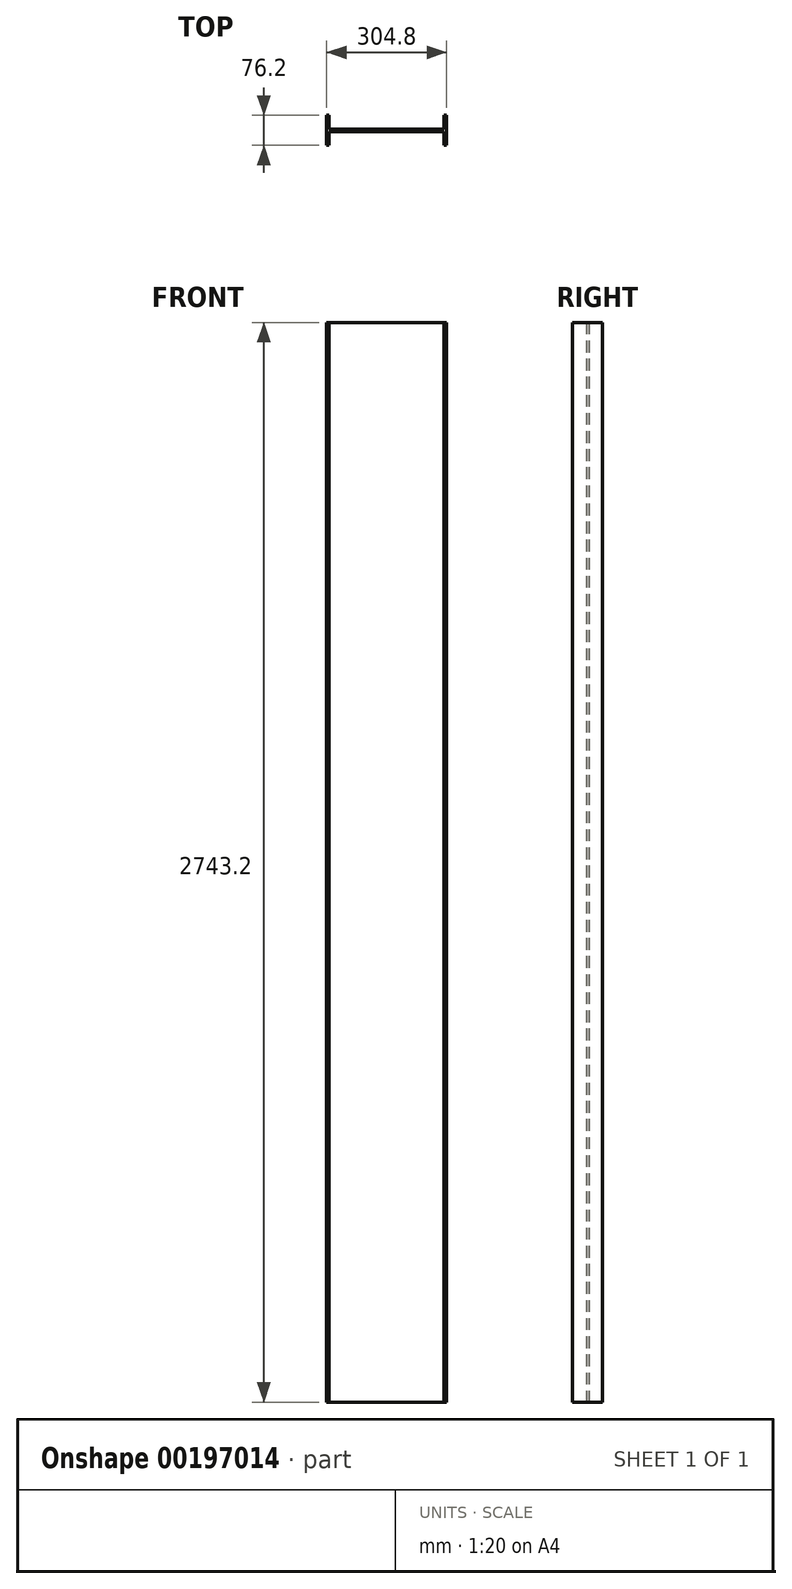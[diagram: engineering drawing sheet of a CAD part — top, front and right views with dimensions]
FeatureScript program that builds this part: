
annotation { "Feature Type Name" : "Feature", "Feature Type Description" : "" }
export const myFeature = defineFeature(function(context is Context, id is Id, definition is map)
    precondition{}
    {
        {
            var Q0;
            Q0=qCreatedBy(makeId("Top.planeOp"),FACE);
            var sketch = newSketch(context, id + "F0", { "sketchPlane" : qUnion([Q0])});
            skLineSegment(sketch, "E0.bottom", {"start": v(0, 0) * mm, "end": v(6.35, 0) * mm});
            skLineSegment(sketch, "E0.top", {"start": v(0, 76.2) * mm, "end": v(6.35, 76.2) * mm});
            skLineSegment(sketch, "E0.left", {"start": v(0, 0) * mm, "end": v(0, 76.2) * mm});
            skLineSegment(sketch, "E0.right", {"start": v(304.8, 0) * mm, "end": v(304.8, 76.2) * mm});
            skLineSegment(sketch, "E1", {"start": v(6.35, 76.2) * mm, "end": v(6.35, 41.28) * mm});
            skLineSegment(sketch, "E2", {"start": v(298.45, 76.2) * mm, "end": v(298.45, 41.28) * mm});
            skLineSegment(sketch, "E3", {"start": v(6.35, 41.28) * mm, "end": v(298.45, 41.28) * mm});
            skLineSegment(sketch, "E4", {"start": v(6.35, 34.93) * mm, "end": v(298.45, 34.93) * mm});
            skLineSegment(sketch, "E5.trimOffspring", {"start": v(298.45, 34.93) * mm, "end": v(298.45, 0) * mm});
            skLineSegment(sketch, "E6.trimOffspring", {"start": v(298.45, 0) * mm, "end": v(304.8, 0) * mm});
            skLineSegment(sketch, "E7.trimOffspring", {"start": v(298.45, 76.2) * mm, "end": v(304.8, 76.2) * mm});
            skLineSegment(sketch, "E8.trimOffspring", {"start": v(6.35, 34.93) * mm, "end": v(6.35, 0) * mm});
            skSolve(sketch);
        }
        {
            var Q0;
            Q0 = qSketchRegion(id + "F0", true);
            extrude(context, id + "F1", {"entities" : qUnion([Q0]), "depth" : 2743.2 * mm});
        }
    });
